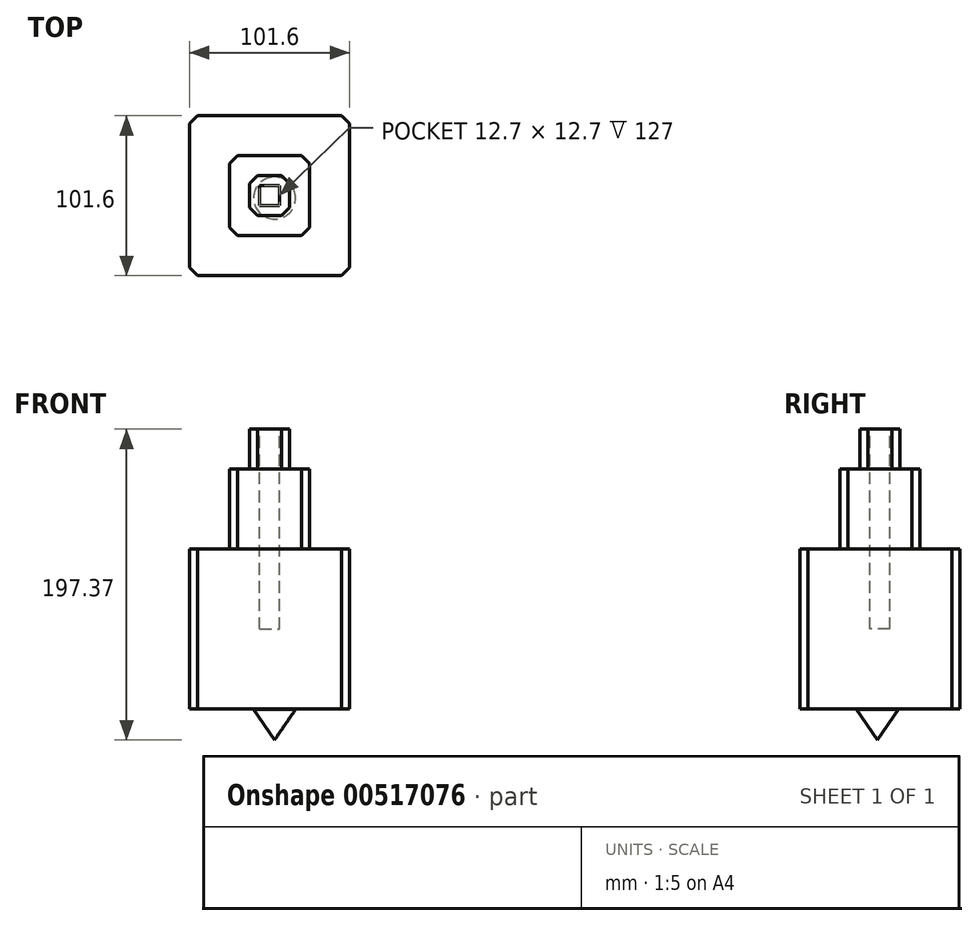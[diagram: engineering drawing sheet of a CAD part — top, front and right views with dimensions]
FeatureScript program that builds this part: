
annotation { "Feature Type Name" : "Feature", "Feature Type Description" : "" }
export const myFeature = defineFeature(function(context is Context, id is Id, definition is map)
    precondition{}
    {
        {
            var Q0;
            Q0=qCreatedBy(makeId("Front.planeOp"),FACE);
            var sketch = newSketch(context, id + "F0", { "sketchPlane" : qUnion([Q0])});
            skLineSegment(sketch, "E0.bottom", {"start": v(-39, 45.25) * mm, "end": v(62.6, 45.25) * mm});
            skLineSegment(sketch, "E0.top", {"start": v(-39, -56.35) * mm, "end": v(62.6, -56.35) * mm});
            skLineSegment(sketch, "E0.left", {"start": v(-39, 45.25) * mm, "end": v(-39, -56.35) * mm});
            skLineSegment(sketch, "E0.right", {"start": v(62.6, 45.25) * mm, "end": v(62.6, -56.35) * mm});
            skSolve(sketch);
        }
        {
            var Q0;
            Q0=makeQuery(id+"F0.imprint","IMPRINT",FACE,{"disambiguationData":[TD([[makeQuery(id+"F0.imprint","IMPRINT",EDGE,{"derivedFrom":sQuery(id+"F0.wireOp",EDGE,"E0.bottom")}),-1.0]])]});
            extrude(context, id + "F1", {"entities" : qUnion([Q0]), "depth" : 101.6 * mm, "offsetDistance" : 25.4 * mm});
        }
        {
            var Q0;
            Q0=makeQuery(id+"F1.opExtrude","SWEPT_FACE",FACE,{"disambiguationData":[OSD([sQuery(id+"F0.wireOp",EDGE,"E0.bottom")])]});
            var sketch = newSketch(context, id + "F2", { "sketchPlane" : qUnion([Q0])});
            skLineSegment(sketch, "E1.bottom", {"start": v(-13.6, -25.4) * mm, "end": v(37.2, -25.4) * mm});
            skLineSegment(sketch, "E1.top", {"start": v(-13.6, -76.2) * mm, "end": v(37.2, -76.2) * mm});
            skLineSegment(sketch, "E1.left", {"start": v(-13.6, -25.4) * mm, "end": v(-13.6, -76.2) * mm});
            skLineSegment(sketch, "E1.right", {"start": v(37.2, -25.4) * mm, "end": v(37.2, -76.2) * mm});
            skSolve(sketch);
        }
        {
            var Q0;
            Q0=makeQuery(id+"F2.imprint","IMPRINT",FACE,{"disambiguationData":[TD([[makeQuery(id+"F2.imprint","IMPRINT",EDGE,{"derivedFrom":sQuery(id+"F2.wireOp",EDGE,"E1.bottom")}),-1.0]])]});
            extrude(context, id + "F3", {"entities" : qUnion([Q0]), "operationType" : NewBodyOperationType.ADD, "depth" : 50.8 * mm, "offsetDistance" : 25.4 * mm});
        }
        {
            var Q0;
            Q0=makeQuery(id+"F3.opExtrude","CAP_FACE",FACE,{"disambiguationData":[OSD([sQuery(id+"F2.wireOp",EDGE,"E1.bottom"),sQuery(id+"F2.wireOp",EDGE,"E1.top"),sQuery(id+"F2.wireOp",EDGE,"E1.left"),sQuery(id+"F2.wireOp",EDGE,"E1.right")])],"isStart":false});
            var sketch = newSketch(context, id + "F4", { "sketchPlane" : qUnion([Q0])});
            skLineSegment(sketch, "E2.bottom", {"start": v(-0.9, -38.1) * mm, "end": v(24.5, -38.1) * mm});
            skLineSegment(sketch, "E2.top", {"start": v(-0.9, -63.5) * mm, "end": v(24.5, -63.5) * mm});
            skLineSegment(sketch, "E2.left", {"start": v(-0.9, -38.1) * mm, "end": v(-0.9, -63.5) * mm});
            skLineSegment(sketch, "E2.right", {"start": v(24.5, -38.1) * mm, "end": v(24.5, -63.5) * mm});
            skPoint(sketch, "E2.middle", {"position": v(11.8, -50.8) * mm});
            skPoint(sketch, "E2.middle.positionSnap0", {"position": v(11.8, -76.2) * mm});
            skPoint(sketch, "E2.centerSnap0", {"position": v(11.8, -76.2) * mm});
            skSolve(sketch);
        }
        {
            var Q0;
            Q0=makeQuery(id+"F4.imprint","IMPRINT",FACE,{"disambiguationData":[TD([[makeQuery(id+"F4.imprint","IMPRINT",EDGE,{"derivedFrom":sQuery(id+"F4.wireOp",EDGE,"E2.bottom")}),-1.0]])]});
            extrude(context, id + "F5", {"entities" : qUnion([Q0]), "operationType" : NewBodyOperationType.ADD, "depth" : 25.4 * mm, "offsetDistance" : 25.4 * mm});
        }
        {
            var Q0;
            Q0=makeQuery(id+"F5.opExtrude","CAP_FACE",FACE,{"disambiguationData":[OSD([sQuery(id+"F4.wireOp",EDGE,"E2.bottom"),sQuery(id+"F4.wireOp",EDGE,"E2.top"),sQuery(id+"F4.wireOp",EDGE,"E2.left"),sQuery(id+"F4.wireOp",EDGE,"E2.right")])],"isStart":false});
            var sketch = newSketch(context, id + "F6", { "sketchPlane" : qUnion([Q0])});
            skLineSegment(sketch, "E3.bottom", {"start": v(5.45, -44.45) * mm, "end": v(18.15, -44.45) * mm});
            skLineSegment(sketch, "E3.top", {"start": v(5.45, -57.15) * mm, "end": v(18.15, -57.15) * mm});
            skLineSegment(sketch, "E3.left", {"start": v(5.45, -44.45) * mm, "end": v(5.45, -57.15) * mm});
            skLineSegment(sketch, "E3.right", {"start": v(18.15, -44.45) * mm, "end": v(18.15, -57.15) * mm});
            skSolve(sketch);
        }
        {
            var Q0;
            Q0=makeQuery(id+"F6.imprint","IMPRINT",FACE,{"disambiguationData":[TD([[makeQuery(id+"F6.imprint","IMPRINT",EDGE,{"derivedFrom":sQuery(id+"F6.wireOp",EDGE,"E3.bottom")}),-1.0]])]});
            extrude(context, id + "F7", {"entities" : qUnion([Q0]), "operationType" : NewBodyOperationType.REMOVE, "oppositeDirection" : true, "depth" : 127 * mm, "offsetDistance" : 25.4 * mm});
        }
        {
            var Q0;
            Q0=makeQuery(id+"F1.opExtrude","CAP_EDGE",EDGE,{"disambiguationData":[OSD([sQuery(id+"F0.wireOp",EDGE,"E0.left")])],"isStart":true});
            var Q1;
            Q1=makeQuery(id+"F1.opExtrude","CAP_EDGE",EDGE,{"disambiguationData":[OSD([sQuery(id+"F0.wireOp",EDGE,"E0.right")])],"isStart":true});
            var Q2;
            Q2=makeQuery(id+"F1.opExtrude","CAP_EDGE",EDGE,{"disambiguationData":[OSD([sQuery(id+"F0.wireOp",EDGE,"E0.right")])],"isStart":false});
            var Q3;
            Q3=makeQuery(id+"F1.opExtrude","CAP_EDGE",EDGE,{"disambiguationData":[OSD([sQuery(id+"F0.wireOp",EDGE,"E0.left")])],"isStart":false});
            chamfer(context, id + "F8", {"entities" : qUnion([Q0, Q1, Q2, Q3]), "width" : 5.08 * mm, "tangentPropagation" : true});
        }
        {
            var Q0;
            Q0=makeQuery(id+"F3.opExtrude","SWEPT_EDGE",EDGE,{"disambiguationData":[OSD([sQuery(id+"F2.wireOp",EDGE,"E1.top"),sQuery(id+"F2.wireOp",EDGE,"E1.right")])]});
            var Q1;
            Q1=makeQuery(id+"F3.opExtrude","SWEPT_EDGE",EDGE,{"disambiguationData":[OSD([sQuery(id+"F2.wireOp",EDGE,"E1.bottom"),sQuery(id+"F2.wireOp",EDGE,"E1.right")])]});
            var Q2;
            Q2=makeQuery(id+"F3.opExtrude","SWEPT_EDGE",EDGE,{"disambiguationData":[OSD([sQuery(id+"F2.wireOp",EDGE,"E1.bottom"),sQuery(id+"F2.wireOp",EDGE,"E1.left")])]});
            var Q3;
            Q3=makeQuery(id+"F3.opExtrude","SWEPT_EDGE",EDGE,{"disambiguationData":[OSD([sQuery(id+"F2.wireOp",EDGE,"E1.top"),sQuery(id+"F2.wireOp",EDGE,"E1.left")])]});
            var Q4;
            Q4=makeQuery(id+"F5.opExtrude","SWEPT_EDGE",EDGE,{"disambiguationData":[OSD([sQuery(id+"F4.wireOp",EDGE,"E2.top"),sQuery(id+"F4.wireOp",EDGE,"E2.left")])]});
            var Q5;
            Q5=makeQuery(id+"F5.opExtrude","SWEPT_EDGE",EDGE,{"disambiguationData":[OSD([sQuery(id+"F4.wireOp",EDGE,"E2.bottom"),sQuery(id+"F4.wireOp",EDGE,"E2.left")])]});
            var Q6;
            Q6=makeQuery(id+"F5.opExtrude","SWEPT_EDGE",EDGE,{"disambiguationData":[OSD([sQuery(id+"F4.wireOp",EDGE,"E2.top"),sQuery(id+"F4.wireOp",EDGE,"E2.right")])]});
            var Q7;
            Q7=makeQuery(id+"F5.opExtrude","SWEPT_EDGE",EDGE,{"disambiguationData":[OSD([sQuery(id+"F4.wireOp",EDGE,"E2.bottom"),sQuery(id+"F4.wireOp",EDGE,"E2.right")])]});
            chamfer(context, id + "F9", {"entities" : qUnion([Q0, Q1, Q2, Q3, Q4, Q5, Q6, Q7]), "width" : 5.08 * mm, "tangentPropagation" : true});
        }
        {
            var Q0;
            Q0=qCreatedBy(makeId("Right.planeOp"),FACE);
            var sketch = newSketch(context, id + "F10", { "sketchPlane" : qUnion([Q0])});
            skLineSegment(sketch, "E4", {"start": v(-66.02, -56.43) * mm, "end": v(-66.02, -75.92) * mm});
            skLineSegment(sketch, "E5", {"start": v(-66.02, -56.43) * mm, "end": v(-52.63, -56.43) * mm});
            skLineSegment(sketch, "E6", {"start": v(-52.63, -56.43) * mm, "end": v(-66.02, -75.92) * mm});
            skSolve(sketch);
        }
        {
            var Q0;
            Q0=makeQuery(id+"F10.imprint","IMPRINT",FACE,{"disambiguationData":[TD([[makeQuery(id+"F10.imprint","IMPRINT",EDGE,{"derivedFrom":sQuery(id+"F10.wireOp",EDGE,"E4")}),1.0]])]});
            var Q1;
            Q1=sQuery(id+"F10.wireOp",EDGE,"E4");
            revolve(context, id + "F11", {"entities" : qUnion([Q0]), "axis" : qUnion([Q1]), "revolveType" : RevolveType.FULL});
        }
        {
            var Q0;
            Q0=makeQuery(id+"F11.opRevolve","SWEPT_BODY",BODY,{"disambiguationData":[OSD([sQuery(id+"F10.wireOp",EDGE,"E4"),sQuery(id+"F10.wireOp",EDGE,"E5"),sQuery(id+"F10.wireOp",EDGE,"E6")])]});
            transform(context, id + "F12", {"entities" : qUnion([Q0]), "transformType" : TransformType.TRANSLATION_3D, "dx" : 15 * mm, "dy" : 13.72 * mm, "dz" : 0 * mm, "makeCopy" : false});
        }
    });
